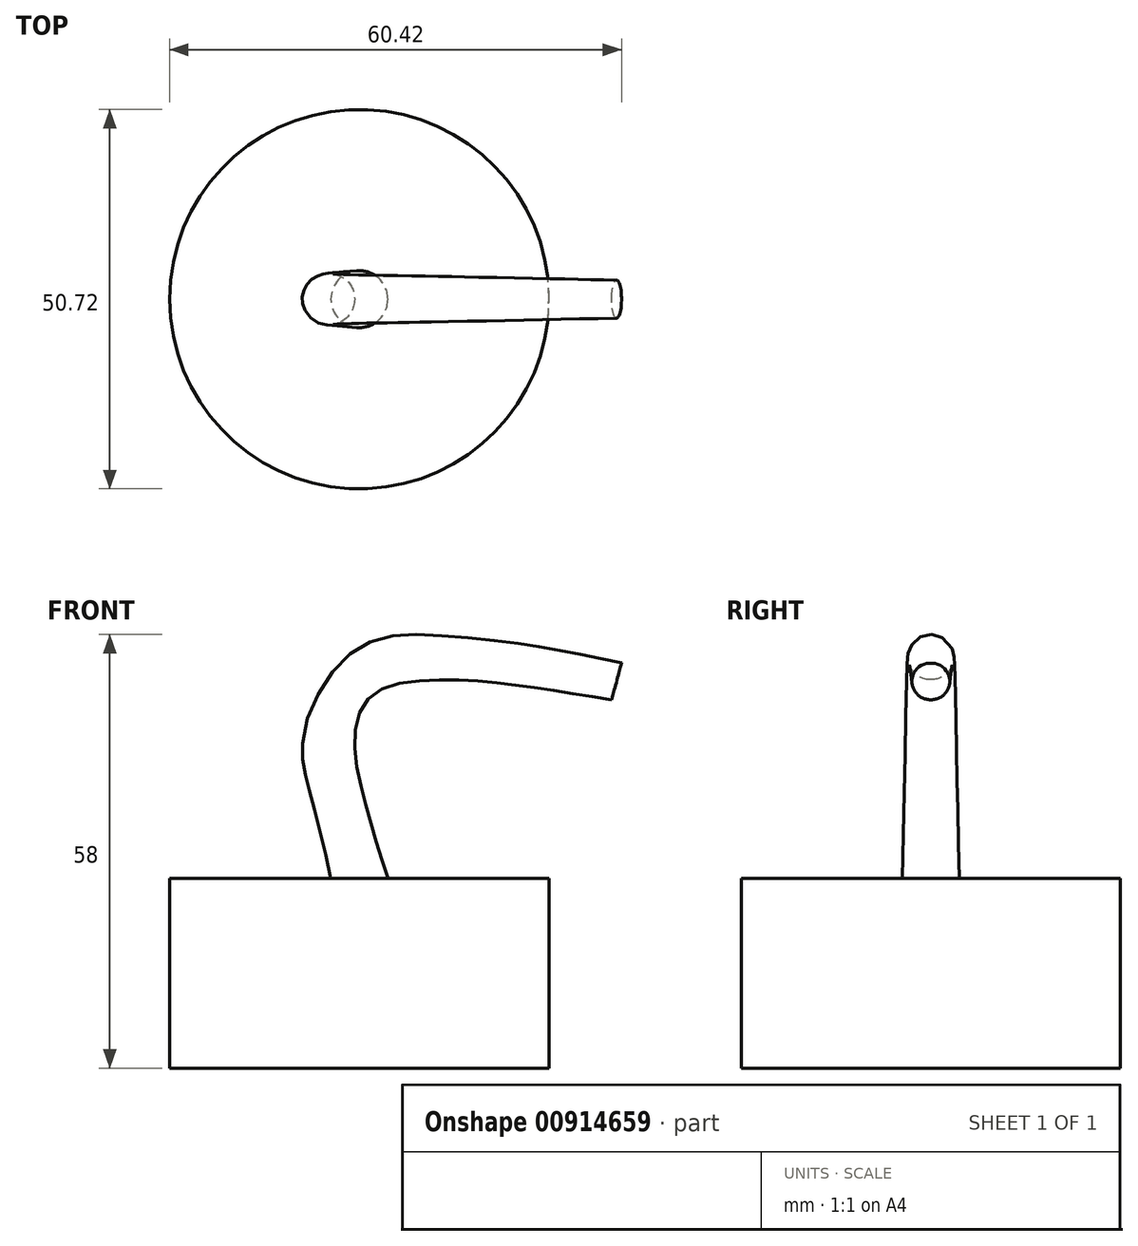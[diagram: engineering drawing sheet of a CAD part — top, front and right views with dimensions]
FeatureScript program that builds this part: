
annotation { "Feature Type Name" : "Feature", "Feature Type Description" : "" }
export const myFeature = defineFeature(function(context is Context, id is Id, definition is map)
    precondition{}
    {
        {
            var Q0;
            Q0=qCreatedBy(makeId("Top.planeOp"),FACE);
            var sketch = newSketch(context, id + "F0", { "sketchPlane" : qUnion([Q0])});
            skCircle(sketch, "E0", {"center": v(0, 0) * mm, "radius": 25.36 * mm});
            skSolve(sketch);
        }
        {
            var Q0;
            Q0=makeQuery(id+"F0.imprint","IMPRINT",FACE,{"disambiguationData":[TD([[makeQuery(id+"F0.imprint","IMPRINT",EDGE,{"derivedFrom":sQuery(id+"F0.wireOp",EDGE,"E0")}),1.0]])]});
            extrude(context, id + "F1", {"entities" : qUnion([Q0]), "depth" : 25.4 * mm, "offsetDistance" : 25.4 * mm});
        }
        {
            var Q0;
            Q0=makeQuery(id+"F1.opExtrude","CAP_FACE",FACE,{"disambiguationData":[OSD([sQuery(id+"F0.wireOp",EDGE,"E0")])],"isStart":false});
            var sketch = newSketch(context, id + "F2", { "sketchPlane" : qUnion([Q0])});
            skCircle(sketch, "E1", {"center": v(0, 0) * mm, "radius": 3.8 * mm});
            skSolve(sketch);
        }
        {
            var Q0;
            Q0=qCreatedBy(makeId("Front.planeOp"),FACE);
            var sketch = newSketch(context, id + "F3", { "sketchPlane" : qUnion([Q0])});
            skFitSpline(sketch, "E2", {"points": [v(0, 24.59) * mm, v(0, 49.99) * mm, v(33.16, 47.14) * mm], "startDerivative": vector(-14.48, 68.42) * mm, "endDerivative": vector(78.7, -21.3) * mm});
            skSolve(sketch);
        }
        {
            var Q0;
            Q0=sQuery(id+"F3.wireOp",VERTEX,"E2.end");
            var Q1;
            Q1=sQuery(id+"F3.wireOp",EDGE,"E2");
            cPlane(context, id + "F4", {"entities" : qUnion([Q0, Q1]), "cplaneType" : CPlaneType.CURVE_POINT, "offset" : 25.4 * mm, "width" : 152.4 * mm, "height" : 152.4 * mm});
        }
        {
            var Q0;
            Q0=qCreatedBy(id+"F4.planeOp",FACE);
            var sketch = newSketch(context, id + "F5", { "sketchPlane" : qUnion([Q0])});
            skCircle(sketch, "E3", {"center": v(0, 58.91) * mm, "radius": 2.54 * mm});
            skSolve(sketch);
        }
        {
            var Q0;
            Q0=sQuery(id+"F3.wireOp",EDGE,"E2");
            var Q2;
            Q2=makeQuery(id+"F5.imprint","IMPRINT",FACE,{"disambiguationData":[TD([[makeQuery(id+"F5.imprint","IMPRINT",EDGE,{"derivedFrom":sQuery(id+"F5.wireOp",EDGE,"E3")}),1.0]])]});
            var Q3;
            Q3=makeQuery(id+"F2.imprint","IMPRINT",FACE,{"disambiguationData":[TD([[makeQuery(id+"F2.imprint","IMPRINT",EDGE,{"derivedFrom":sQuery(id+"F2.wireOp",EDGE,"E1")}),1.0]])]});
            loft(context, id + "F6", {"operationType" : NewBodyOperationType.ADD, "addSections" : true, "spine" : qUnion([Q0]), "sectionCount" : 5, "sheetProfilesArray" : [{ "sheetProfileEntities" : qUnion([Q2]) }, { "sheetProfileEntities" : qUnion([Q3]) }]});
        }
    });
